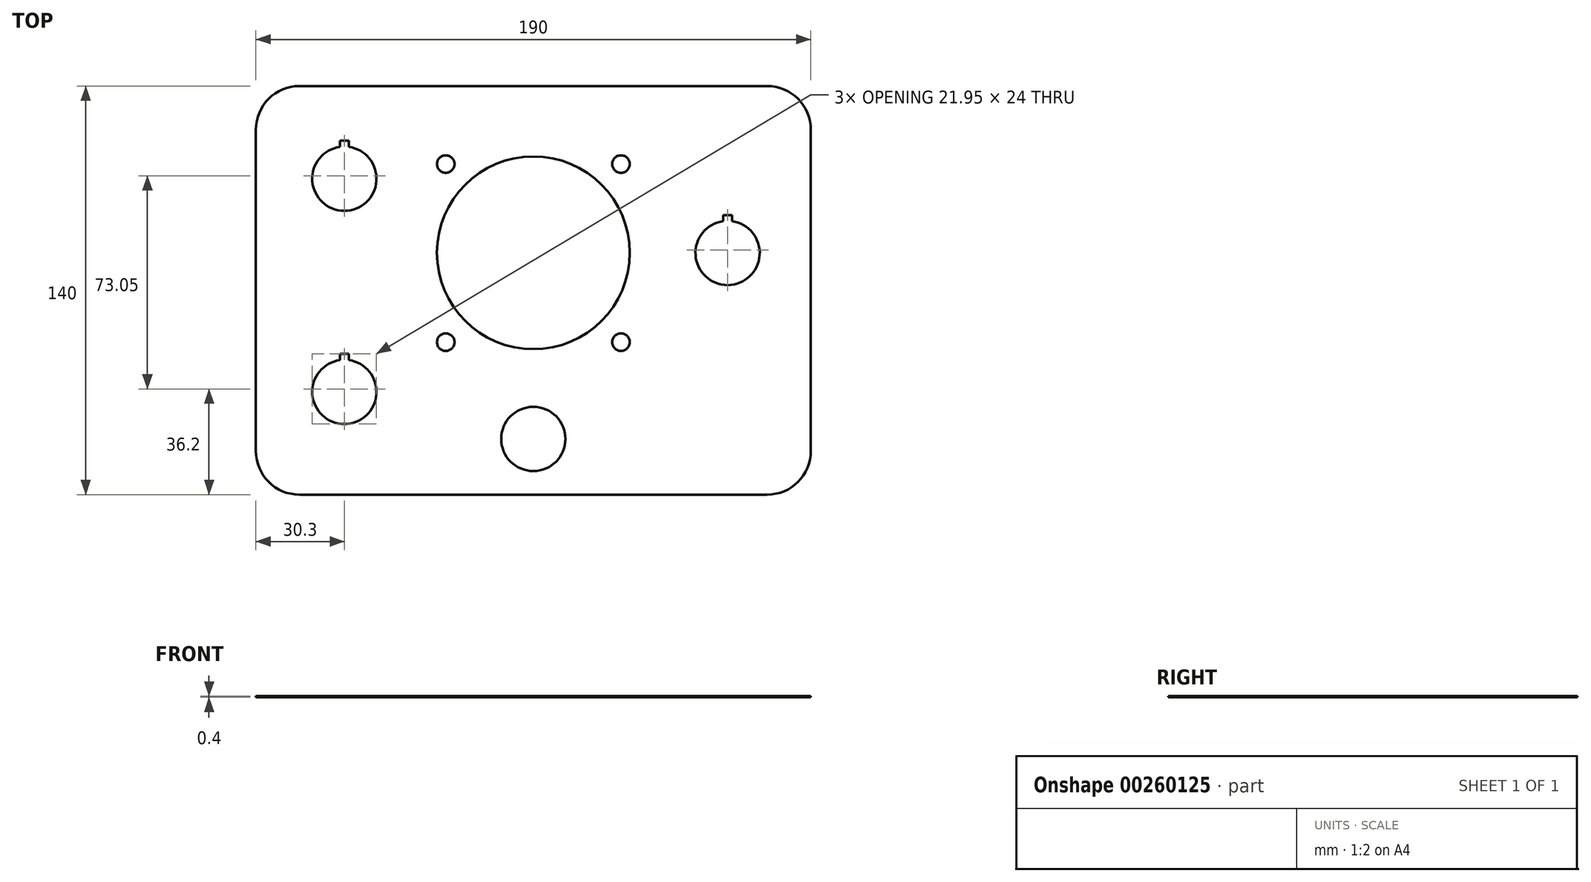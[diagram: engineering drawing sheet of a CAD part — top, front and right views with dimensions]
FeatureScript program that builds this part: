
annotation { "Feature Type Name" : "Feature", "Feature Type Description" : "" }
export const myFeature = defineFeature(function(context is Context, id is Id, definition is map)
    precondition{}
    {
        {
            var Q0;
            Q0=qCreatedBy(makeId("Top.planeOp"),FACE);
            var sketch = newSketch(context, id + "F0", { "sketchPlane" : qUnion([Q0])});
            skLineSegment(sketch, "E0.bottom", {"start": v(15, 0) * mm, "end": v(175, 0) * mm});
            skLineSegment(sketch, "E0.top", {"start": v(15, 140) * mm, "end": v(175, 140) * mm});
            skLineSegment(sketch, "E0.left", {"start": v(0, 15) * mm, "end": v(0, 125) * mm});
            skLineSegment(sketch, "E0.right", {"start": v(190, 15) * mm, "end": v(190, 125) * mm});
            skCircle(sketch, "E1", {"center": v(30.3, 108.25) * mm, "radius": 11 * mm});
            skCircle(sketch, "E2", {"center": v(30.3, 35.2) * mm, "radius": 11 * mm});
            skCircle(sketch, "E3", {"center": v(95, 19.1) * mm, "radius": 11 * mm});
            skCircle(sketch, "E4", {"center": v(161.5, 82.8) * mm, "radius": 11 * mm});
            skCircle(sketch, "E5", {"center": v(95, 82.85) * mm, "radius": 33 * mm});
            skCircle(sketch, "E6", {"center": v(65, 113.25) * mm, "radius": 3 * mm});
            skCircle(sketch, "E7", {"center": v(65, 52.25) * mm, "radius": 3 * mm});
            skCircle(sketch, "E8", {"center": v(125, 52.25) * mm, "radius": 3 * mm});
            skCircle(sketch, "E9", {"center": v(125, 113.25) * mm, "radius": 3 * mm});
            skPoint(sketch, "E10.visualSharp", {"position": v(0, 140) * mm});
            skArc(sketch, "E10.filletArc", {"start": v(15, 140) * mm, "mid": v(4.4, 135.6) * mm, "end": v(0, 125) * mm});
            skPoint(sketch, "E11.visualSharp", {"position": v(190, 140) * mm});
            skArc(sketch, "E11.filletArc", {"start": v(190, 125) * mm, "mid": v(185.6, 135.6) * mm, "end": v(175, 140) * mm});
            skPoint(sketch, "E12.visualSharp", {"position": v(190, 0) * mm});
            skArc(sketch, "E12.filletArc", {"start": v(175, 0) * mm, "mid": v(185.6, 4.4) * mm, "end": v(190, 15) * mm});
            skPoint(sketch, "E13.visualSharp", {"position": v(0, 0) * mm});
            skArc(sketch, "E13.filletArc", {"start": v(0, 15) * mm, "mid": v(4.4, 4.4) * mm, "end": v(15, 0) * mm});
            skLineSegment(sketch, "E14.bottom", {"start": v(30.3, 108.25) * mm, "end": v(31.8, 108.25) * mm});
            skLineSegment(sketch, "E14.top", {"start": v(30.3, 121.25) * mm, "end": v(31.8, 121.25) * mm});
            skLineSegment(sketch, "E14.left", {"start": v(30.3, 108.25) * mm, "end": v(30.3, 121.25) * mm});
            skLineSegment(sketch, "E14.right", {"start": v(31.8, 108.25) * mm, "end": v(31.8, 121.25) * mm});
            skLineSegment(sketch, "E15.bottom", {"start": v(30.3, 108.25) * mm, "end": v(28.8, 108.25) * mm});
            skLineSegment(sketch, "E15.top", {"start": v(30.3, 121.25) * mm, "end": v(28.8, 121.25) * mm});
            skLineSegment(sketch, "E15.right", {"start": v(28.8, 108.25) * mm, "end": v(28.8, 121.25) * mm});
            skLineSegment(sketch, "E16.bottom", {"start": v(30.3, 35.2) * mm, "end": v(31.8, 35.2) * mm});
            skLineSegment(sketch, "E16.top", {"start": v(30.3, 48.2) * mm, "end": v(31.8, 48.2) * mm});
            skLineSegment(sketch, "E16.left", {"start": v(30.3, 35.2) * mm, "end": v(30.3, 48.2) * mm});
            skLineSegment(sketch, "E16.right", {"start": v(31.8, 35.2) * mm, "end": v(31.8, 48.2) * mm});
            skLineSegment(sketch, "E17.bottom", {"start": v(30.3, 35.2) * mm, "end": v(28.8, 35.2) * mm});
            skLineSegment(sketch, "E17.top", {"start": v(30.3, 48.2) * mm, "end": v(28.8, 48.2) * mm});
            skLineSegment(sketch, "E17.right", {"start": v(28.8, 35.2) * mm, "end": v(28.8, 48.2) * mm});
            skLineSegment(sketch, "E18.bottom", {"start": v(161.5, 82.8) * mm, "end": v(163, 82.8) * mm});
            skLineSegment(sketch, "E18.top", {"start": v(161.5, 95.8) * mm, "end": v(163, 95.8) * mm});
            skLineSegment(sketch, "E18.left", {"start": v(161.5, 82.8) * mm, "end": v(161.5, 95.8) * mm});
            skLineSegment(sketch, "E18.right", {"start": v(163, 82.8) * mm, "end": v(163, 95.8) * mm});
            skLineSegment(sketch, "E19.bottom", {"start": v(161.5, 82.8) * mm, "end": v(161.5, 82.8) * mm});
            skLineSegment(sketch, "E19.top", {"start": v(161.5, 95.8) * mm, "end": v(161.5, 95.8) * mm});
            skLineSegment(sketch, "E20.bottom", {"start": v(161.5, 82.8) * mm, "end": v(160, 82.8) * mm});
            skLineSegment(sketch, "E20.top", {"start": v(161.5, 95.8) * mm, "end": v(160, 95.8) * mm});
            skLineSegment(sketch, "E20.right", {"start": v(160, 82.8) * mm, "end": v(160, 95.8) * mm});
            skSolve(sketch);
        }
        {
            var Q0;
            Q0=makeQuery(id+"F0.imprint","IMPRINT",FACE,{"disambiguationData":[TD([[makeQuery(id+"F0.imprint","IMPRINT",EDGE,{"derivedFrom":sQuery(id+"F0.wireOp",EDGE,"E0.bottom")}),1.0]])]});
            extrude(context, id + "F1", {"entities" : qUnion([Q0]), "depth" : .4 * mm});
        }
    });
